FCSTD DOCUMENT  (FreeCAD 0.21R33771 (Git))
Label: Master_of_Puppets
License: All rights reserved
LicenseURL: https://en.wikipedia.org/wiki/All_rights_reserved
objects: Spreadsheet::Sheet×10

FEATURE [Spreadsheet::Sheet] Spreadsheet
  cells = A1='MagnAFPM; A2='RotorDiameter; B2(RotorDiameter)=1200; A3='RotorDiskRadius; B3(RotorDiskRadius)=80.05; A4='RotorDiskInnerRadius; B4(RotorDiskInnerRadius)=54.89; A5='RotorDiskThickness; B5(RotorDiskThickness)=5; A6='MagnetLength; B6(MagnetLength)=25; A7='MagnetWidth; B7(MagnetWidth)=10; A8='MagnetThickness; B8(MagnetThickness)=8; A9='MagnetMaterial; B9(MagnetMaterial)='Neodymium; A10='NumberMagnet; B10(NumberMagnet)=16; A11='StatorThickness; B11(StatorThickness)=8; A12='CoilType; B12(CoilType)=1; A13='CoilLegWidth; B13(CoilLegWidth)=9.36; A14='CoilHoleWidthAtOuterRadius; B14(CoilHoleWidthAtOuterRadius)=10; A15='CoilHoleWidthAtInnerRadius; B15(CoilHoleWidthAtInnerRadius)=10; A16='MechanicalClearance; B16(MechanicalClearance)=3; A17='InnerDistanceBetweenMagnets; B17(InnerDistanceBetweenMagnets)=11.56; A18='NumberOfCoilsPerPhase; B18(NumberOfCoilsPerPhase)=4; A19='WireWeight; B19(WireWeight)=0.46; A20='WireDiameter; B20(WireDiameter)=0.71; A21='NumberOfWiresInHand; B21(NumberOfWiresInHand)=1; A22='TurnsPerCoil; B22(TurnsPerCoil)=103; A23='Furling; A24='VerticalPlaneAngle; B24(VerticalPlaneAngle)=15; A25='HorizontalPlaneAngle; B25(HorizontalPlaneAngle)=55; A26='BracketLength; B26(BracketLength)=150; A27='BracketWidth; B27(BracketWidth)=20; A28='BracketThickness; B28(BracketThickness)=5; A29='BoomLength; B29(BoomLength)=700; A30='BoomPipeDiameter; B30(BoomPipeDiameter)=33.4; A31='BoomPipeThickness; B31(BoomPipeThickness)=3; A32='VaneThickness; B32(VaneThickness)=6; A33='VaneLength; B33(VaneLength)=500; A34='VaneWidth; B34(VaneWidth)=200; A35='Offset; B35(Offset)=69; A36='User; A37='BladeWidth; B37(BladeWidth)=140; A38='HubPitchCircleDiameter; B38(HubPitchCircleDiameter)=50; A39='RotorDiskCentralHoleDiameter; B39(RotorDiskCentralHoleDiameter)=35; A40='HolesDiameter; B40(HolesDiameter)=8; A41='MetalLengthL; B41(MetalLengthL)=40; A42='MetalThicknessL; B42(MetalThicknessL)=5; A43='FlatMetalThickness; B43(FlatMetalThickness)=5; A44='YawPipeDiameter; B44(YawPipeDiameter)=48.3; A45='PipeThickness; B45(PipeThickness)=3; A46='RotorResinMargin; B46(RotorResinMargin)=5; A47='HubHolesDiameter; B47(HubHolesDiameter)=8
FEATURE [Spreadsheet::Sheet] Fastener
  cells = A1='Inputs; A2='BracketThickness; B2(BracketThickness)==Spreadsheet.BracketThickness; A3='VaneThickness; B3(VaneThickness)==Spreadsheet.VaneThickness; A4='FlatMetalThickness; B4(FlatMetalThickness)==Spreadsheet.FlatMetalThickness; A5='HolesDiameter; B5(HolesDiameter)==Spreadsheet.HolesDiameter; A6='HubHolesDiameter; B6(HubHolesDiameter)==Spreadsheet.HubHolesDiameter; A7='Static; A8='HolesRadius; B8(HolesRadius)==HolesDiameter / 2; A9='HubHolesRadius; B9(HubHolesRadius)==HubHolesDiameter / 2; A10='HexNutThickness; B10(HexNutThickness)==1.64 * HolesRadius + 0.35; A11='HubHexNutThickness; B11(HubHexNutThickness)==1.64 * HubHolesRadius + 0.35; A12='WasherThickness; B12(WasherThickness)=2.5; A13='DistanceThreadsExtendFromNuts; B13(DistanceThreadsExtendFromNuts)=5; A14='HubHolesBoltLength; B14(HubHolesBoltLength)=50; A15='WoodScrewDiameter; B15(WoodScrewDiameter)=5; A16='ScrewHoleDiameter; B16(ScrewHoleDiameter)==WoodScrewDiameter - 1; A17='Calculated; A18='UnroundedTailVaneBracketBoltLength; B18(UnroundedTailVaneBracketBoltLength)==BracketThickness + VaneThickness + FlatMetalThickness + DistanceThreadsExtendFromNuts + WasherThickness; A19='TailVaneBracketBoltLength; B19(TailVaneBracketBoltLength)==UnroundedTailVaneBracketBoltLength + 5 - mod(UnroundedTailVaneBracketBoltLength; 5); A20='HolesWidthAcrossCorners; B20='Select C (MAX) based on HolesRadius.; C20='https://www.atlrod.com/metric-hex-bolt-dimensions/; A21='HWACrange7; B21(HWACrange7)==HolesRadius <= 18 ? 63.51 : 75.05; A22='HWACrange6; B22(HWACrange6)==HolesRadius <= 15 ? 53.12 : HWACrange7; A23='HWACrange5; B23(HWACrange5)==HolesRadius <= 12 ? 41.57 : HWACrange6; A24='HWACrange4; B24(HWACrange4)==HolesRadius <= 10 ? 34.64 : HWACrange5; A25='HWACrange3; B25(HWACrange3)==HolesRadius <= 8 ? 27.71 : HWACrange4; A26='HWACrange2; B26(HWACrange2)==HolesRadius <= 7 ? 24.25 : HWACrange3; A27='HWACrange1; B27(HWACrange1)==HolesRadius <= 6 ? 20.78 : HWACrange2; A28='HolesWidthAcrossCorners; B28(HolesWidthAcrossCorners)==HolesRadius <= 5 ? 18.48 : HWACrange1; A29='HubHolesWidthAcrossCorners; B29='Select C (MAX) based on HubHolesRadius.; C29='https://www.atlrod.com/metric-hex-bolt-dimensions/; A30='HHWACrange7; B30(HHWACrange7)==HubHolesRadius <= 18 ? 63.51 : 75.05; A31='HHWACrange6; B31(HHWACrange6)==HubHolesRadius <= 15 ? 53.12 : HHWACrange7; A32='HHWACrange5; B32(HHWACrange5)==HubHolesRadius <= 12 ? 41.57 : HHWACrange6; A33='HHWACrange4; B33(HHWACrange4)==HubHolesRadius <= 10 ? 34.64 : HHWACrange5; A34='HHWACrange3; B34(HHWACrange3)==HubHolesRadius <= 8 ? 27.71 : HHWACrange4; A35='HHWACrange2; B35(HHWACrange2)==HubHolesRadius <= 7 ? 24.25 : HHWACrange3; A36='HHWACrange1; B36(HHWACrange1)==HubHolesRadius <= 6 ? 20.78 : HHWACrange2; A37='HubHolesWidthAcrossCorners; B37(HubHolesWidthAcrossCorners)==HubHolesRadius <= 5 ? 18.48 : HHWACrange1
FEATURE [Spreadsheet::Sheet] Hub
  cells = A1='Inputs; A2='Spreadsheet; A3='RotorDiskRadius; B3='HubPitchCircleDiameter; C3='HubHolesDiameter; A4(RotorDiskRadius)==Spreadsheet.RotorDiskRadius; B4(HubPitchCircleDiameter)==Spreadsheet.HubPitchCircleDiameter; C4(HubHolesDiameter)==Spreadsheet.HubHolesDiameter; A5='MetalLengthL; B5='RotorDiskCentralHoleDiameter; A6(MetalLengthL)==Spreadsheet.MetalLengthL; B6(RotorDiskCentralHoleDiameter)==Spreadsheet.RotorDiskCentralHoleDiameter; A7='Fastener; A8='HubHexNutThickness; A9(HubHexNutThickness)==Fastener.HubHexNutThickness; A10='Common; A11='CoverThickness; A12(CoverThickness)=10; A13='Calculated; A14='RotorDiskCentralHoleRadius; B14='HubHolesRadius; C14='HubPitchCircleRadius; A15(RotorDiskCentralHoleRadius)==RotorDiskCentralHoleDiameter / 2; B15(HubHolesRadius)==HubHolesDiameter / 2; C15(HubPitchCircleRadius)==HubPitchCircleDiameter / 2; A16='Dimensions; D17='FrameSidePad; F17='RotorSidePad; B18='MiddlePadRadiusMargin; C18='ProtrudingPadThickness; D18='Radius; E18='Width; F18='Radius; G18='Width; H18='NumberOfHoles; I18='StubAxleShaftRadius; A19='TShape; B19(TShapeMiddlePadRadiusMargin)=15; C19(TShapeProtrudingPadThickness)=5; D19(TShapeFrameSidePadRadius)=32.5; E19(TShapeFrameSidePadWidth)=45; F19(TShapeRotorSidePadRadius)=28; G19(TShapeRotorSidePadWidth)=40; H19(TShapeNumberOfHoles)=4; I19(TShapeStubAxleShaftRadius)=18; A20='HShape; B20(HShapeMiddlePadRadiusMargin)=15; C20(HShapeProtrudingPadThickness)=5; D20(HShapeFrameSidePadRadius)=42.5; E20(HShapeFrameSidePadWidth)=45; F20(HShapeRotorSidePadRadius)=31; G20(HShapeRotorSidePadWidth)=40; H20(HShapeNumberOfHoles)=5; I20(HShapeStubAxleShaftRadius)=22.5; A21='StarShape; B21(StarShapeMiddlePadRadiusMargin)=20; C21(StarShapeProtrudingPadThickness)=10; D21(StarShapeFrameSidePadRadius)=52.5; E21(StarShapeFrameSidePadWidth)=55; F21(StarShapeRotorSidePadRadius)=47.5; G21(StarShapeRotorSidePadWidth)=75; H21(StarShapeNumberOfHoles)=6; I21(StarShapeStubAxleShaftRadius)=30; A22='Default Value; B22(MiddlePadRadiusMargin)==RotorDiskRadius < 187.5 ? TShapeMiddlePadRadiusMargin : (RotorDiskRadius < 275 ? HShapeMiddlePadRadiusMargin : StarShapeMiddlePadRadiusMargin); C22(ProtrudingPadThickness)==RotorDiskRadius < 187.5 ? TShapeProtrudingPadThickness : (RotorDiskRadius < 275 ? HShapeProtrudingPadThickness : StarShapeProtrudingPadThickness); D22(FrameSidePadRadius)==RotorDiskRadius < 187.5 ? TShapeFrameSidePadRadius : (RotorDiskRadius < 275 ? HShapeFrameSidePadRadius : StarShapeFrameSidePadRadius); E22(FrameSidePadWidth)==RotorDiskRadius < 187.5 ? TShapeFrameSidePadWidth : (RotorDiskRadius < 275 ? HShapeFrameSidePadWidth : StarShapeFrameSidePadWidth); F22(DefaultRotorSidePadRadius)==RotorDiskRadius < 187.5 ? TShapeRotorSidePadRadius : (RotorDiskRadius < 275 ? HShapeRotorSidePadRadius : StarShapeRotorSidePadRadius); G22(RotorSidePadWidth)==RotorDiskRadius < 187.5 ? TShapeRotorSidePadWidth : (RotorDiskRadius < 275 ? HShapeRotorSidePadWidth : StarShapeRotorSidePadWidth); H22(NumberOfHoles)==RotorDiskRadius < 187.5 ? TShapeNumberOfHoles : (RotorDiskRadius < 275 ? HShapeNumberOfHoles : StarShapeNumberOfHoles); I22(StubAxleShaftRadius)==RotorDiskRadius < 187.5 ? TShapeStubAxleShaftRadius : (RotorDiskRadius < 275 ? HShapeStubAxleShaftRadius : StarShapeStubAxleShaftRadius); A23='Value; F23(RotorSidePadRadius)==DefaultRotorSidePadRadius >= RotorDiskCentralHoleRadius ? RotorDiskCentralHoleRadius - 3 : DefaultRotorSidePadRadius; A24='MiddlePad; A25='Radius; B25='Thickness; A26(MiddlePadRadius)==HubPitchCircleRadius + HubHolesRadius + MiddlePadRadiusMargin; B26(MiddlePadThickness)=16; A27='StubAxleShaft; A28='LengthOfTwoNuts; B28='DistanceStubAxleShaftExtendsBeyondTheFrame; C28='DistanceBetweenFrameAndBackRotor; D28='Length; A29(LengthOfTwoNuts)==HubHexNutThickness * 2; B29(DistanceStubAxleShaftExtendsBeyondTheFrame)=20; C29(DistanceBetweenFrameAndBackRotor)==MiddlePadThickness + LengthOfTwoNuts; D29(StubAxleShaftLength)==DistanceBetweenFrameAndBackRotor + MetalLengthL + DistanceStubAxleShaftExtendsBeyondTheFrame
FEATURE [Spreadsheet::Sheet] Blade
  cells = A1='Inputs; A2='Spreadsheet; A3='RotorDiameter; B3='BladeWidth; C3='HubPitchCircleDiameter; A4(RotorDiameter)==Spreadsheet.RotorDiameter; B4(BladeWidth)==Spreadsheet.BladeWidth; C4(HubPitchCircleDiameter)==Spreadsheet.HubPitchCircleDiameter; A5='HubHolesDiameter; B5='ScrewHoleDiameter; A6(HubHolesDiameter)==Spreadsheet.HubHolesDiameter; B6(ScrewHoleDiameter)==Fastener.ScrewHoleDiameter; A7='Static; A8='BladeTemplateThickness; A9(BladeTemplateThickness)=6; A10='Calculated; A11='HubPitchCircleRadius; B11='HubHolesRadius; C11='ScrewHoleRadius; A12(HubPitchCircleRadius)==HubPitchCircleDiameter / 2; B12(HubHolesRadius)==HubHolesDiameter / 2; C12(ScrewHoleRadius)==ScrewHoleDiameter / 2; A13='BladeRadius; B13='MinimumBladeWidth; A14(BladeRadius)==RotorDiameter / 2; B14(MinimumBladeWidth)==max(round(0.055 * RotorDiameter - 8); 95); A15='BladeAssemblyBackDiskDiameter; B15='BladeAssemblyFrontTriangleSideLength; A16(BladeAssemblyBackDiskDiameter)==max(round(0.106 * RotorDiameter - 3.121); 200); B16(BladeAssemblyFrontTriangleSideLength)==max(round(0.147 * RotorDiameter + 6.213); 274); A17='BladeTemplateDim_V; B17='BladeTemplateDim_W; A18(BladeTemplateDim_V)==max(round(0.086 * RotorDiameter - 10.669); 140); B18(BladeTemplateDim_W)==round(0.018 * RotorDiameter + 12.986); A19='UnroundedBladeAssemblyPlateThickness; A20(UnroundedBladeAssemblyPlateThickness)==0.004 * RotorDiameter + 2.426; A21='BladeAssemblyPlateThickness; B21='Round to nearest plywood thickness; A22='Range7; B22(Range7)==UnroundedBladeAssemblyPlateThickness < 28.5 ? 27 : 30; A23='Range6; B23(Range6)==UnroundedBladeAssemblyPlateThickness < 25.5 ? 24 : Range7; A24='Range5; B24(Range5)==UnroundedBladeAssemblyPlateThickness < 22.5 ? 21 : Range6; A25='Range4; B25(Range4)==UnroundedBladeAssemblyPlateThickness < 19.5 ? 18 : Range5; A26='Range3; B26(Range3)==UnroundedBladeAssemblyPlateThickness < 16.5 ? 15 : Range4; A27='Range2; B27(Range2)==UnroundedBladeAssemblyPlateThickness < 13.5 ? 12 : Range3; A28='BladeAssemblyPlateThickness; B28(BladeAssemblyPlateThickness)==UnroundedBladeAssemblyPlateThickness < 10.5 ? 9 : Range2; A29='TotalNumberOfBladeScrews; B29='UnroundedMinimumNumberOfFrontTriangleScrews; C29='UnroundedNumberOfBackDiskScrews; A30(TotalNumberOfBladeScrews)==max(round(0.013 * RotorDiameter + 16.929); 42); B30(UnroundedMinimumNumberOfFrontTriangleScrews)==TotalNumberOfBladeScrews * 0.48; C30(UnroundedNumberOfBackDiskScrews)==TotalNumberOfBladeScrews - UnroundedMinimumNumberOfFrontTriangleScrews; A31='MinimumNumberOfFrontTriangleScrews; B31='NumberOfBackDiskScrews; A32(MinimumNumberOfFrontTriangleScrews)==UnroundedMinimumNumberOfFrontTriangleScrews + 3 - mod(UnroundedMinimumNumberOfFrontTriangleScrews; 3); B32(NumberOfBackDiskScrews)==UnroundedNumberOfBackDiskScrews + 3 - mod(UnroundedNumberOfBackDiskScrews; 3); A33='MinimumNumberOfFrontTriangleScrewsPerBlade; B33='NumberOfBackDiskScrewsPerBlade; A34(MinimumNumberOfFrontTriangleScrewsPerBlade)==MinimumNumberOfFrontTriangleScrews / 3; B34(NumberOfBackDiskScrewsPerBlade)==NumberOfBackDiskScrews / 3; A35='LessThan3000; B35='GreaterThanOrEqualTo3000; C35='BladeThickness; A36(LessThan3000)==round(RotorDiameter * 0.0083333333333 + 20); B36(GreaterThanOrEqualTo3000)==round(RotorDiameter * 0.025 - 30); C36(BladeThickness)==max(RotorDiameter < 3000 ? LessThan3000 : GreaterThanOrEqualTo3000; 35); A37='UnroundedBladeAssemblyScrewLength; B37='BladeAssemblyScrewLength; A38(UnroundedBladeAssemblyScrewLength)==(BladeAssemblyPlateThickness * 2 + BladeThickness) / 2; B38(BladeAssemblyScrewLength)==round(UnroundedBladeAssemblyScrewLength - mod(UnroundedBladeAssemblyScrewLength; 5)); A39='Front Triangle Screw Calculations; A40='DistanceFromCenter; B40(DistanceFromCenter)==BladeWidth - BladeTemplateDim_W; A41='MinimumDistanceFromCenter; B41(MinimumDistanceFromCenter)==MinimumBladeWidth - BladeTemplateDim_W; A42='HalfScrewsPerBlade; B42(HalfScrewsPerBlade)==round(MinimumNumberOfFrontTriangleScrewsPerBlade * 0.5); A43='MinimumNumberOfInnerScrews; B43(MinimumNumberOfInnerScrews)==min(HalfScrewsPerBlade; MinimumNumberOfFrontTriangleScrewsPerBlade - HalfScrewsPerBlade); A44='MinimumNumberOfOuterScrews; B44(MinimumNumberOfOuterScrews)==MinimumNumberOfFrontTriangleScrewsPerBlade - MinimumNumberOfInnerScrews; A45='TriangleHeight; B45(TriangleHeight)==BladeAssemblyFrontTriangleSideLength * sqrt(3) / 2; A46='InscribedCircleRadius; B46(InscribedCircleRadius)==TriangleHeight / 3; A47='LargeDistanceBetweenScrewHolesCircumradii; B47='SmallDistanceBetweenScrewHolesCircumradii; A48(LargeDistanceBetweenScrewHolesCircumradii)==(InscribedCircleRadius - ScrewHoleRadius - (HubPitchCircleRadius + HubHolesRadius)) / 3; B48(SmallDistanceBetweenScrewHolesCircumradii)==(InscribedCircleRadius - ScrewHoleRadius - HubPitchCircleRadius) / 2; A49='TriangleCenterToVertexDistance; B49(TriangleCenterToVertexDistance)==TriangleHeight * 2 / 3; A50='LargeInnerScrewLineDistanceFromCenter; B50='SmallInnerScrewLineDistanceFromCenter; A51(LargeInnerScrewLineDistanceFromCenter)==HubPitchCircleRadius + HubHolesRadius + LargeDistanceBetweenScrewHolesCircumradii; B51(SmallInnerScrewLineDistanceFromCenter)==HubPitchCircleRadius; A52='LargeOuterScrewLineDistanceFromCenter; B52='SmallOuterScrewLineDistanceFromCenter; A53(LargeOuterScrewLineDistanceFromCenter)==LargeInnerScrewLineDistanceFromCenter + ScrewHoleRadius + LargeDistanceBetweenScrewHolesCircumradii; B53(SmallOuterScrewLineDistanceFromCenter)==SmallInnerScrewLineDistanceFromCenter + ScrewHoleRadius + SmallDistanceBetweenScrewHolesCircumradii; A54='DistanceBetweenOuterScrewAndEdge; B54(DistanceBetweenOuterScrewAndEdge)==InscribedCircleRadius - (LargeOuterScrewLineDistanceFromCenter + ScrewHoleRadius); A55='HideInnerScrews; B55(HideInnerScrews)==DistanceBetweenOuterScrewAndEdge < 10 ? 1 : 0; A56='InnerScrewLineDistanceFromCenter; B56(InnerScrewLineDistanceFromCenter)==HideInnerScrews == 1 ? SmallInnerScrewLineDistanceFromCenter : LargeInnerScrewLineDistanceFromCenter; A57='OuterScrewLineDistanceFromCenter; B57(OuterScrewLineDistanceFromCenter)==HideInnerScrews == 1 ? SmallOuterScrewLineDistanceFromCenter : LargeOuterScrewLineDistanceFromCenter; A58='Alpha; B58(Alpha)==acos(BladeTemplateDim_W / TriangleCenterToVertexDistance); A59='Beta; B59(Beta)==180 deg - 60 deg - Alpha; A60='Gamma; B60(Gamma)==180 deg - 90 deg - Beta; A61='InnerScrewBetaHypotenuse; B61(InnerScrewBetaHypotenuse)==InnerScrewLineDistanceFromCenter / cos(Beta); C61='OuterScrewBetaHypotenuse; D61(OuterScrewBetaHypotenuse)==OuterScrewLineDistanceFromCenter / cos(Beta); A62='InnerScrewLineTriangle_Adjacent; B62(InnerScrewLineTriangle_Adjacent)==InnerScrewBetaHypotenuse + BladeTemplateDim_W; C62='OuterScrewLineTriangle_Adjacent; D62(OuterScrewLineTriangle_Adjacent)==OuterScrewBetaHypotenuse + BladeTemplateDim_W; A63='InnerScrewLineTriangle_Hypotenuse; B63(InnerScrewLineTriangle_Hypotenuse)==InnerScrewLineTriangle_Adjacent / cos(Gamma); C63='OuterScrewLineTriangle_Hypotenuse; D63(OuterScrewLineTriangle_Hypotenuse)==OuterScrewLineTriangle_Adjacent / cos(Gamma); A64='InnerScrewGammaAdjacent; B64(InnerScrewGammaAdjacent)==max(InnerScrewBetaHypotenuse - DistanceFromCenter; 0); C64='OuterScrewGammaAdjacent; D64(OuterScrewGammaAdjacent)==max(OuterScrewBetaHypotenuse - DistanceFromCenter; 0); A65='InnerScrewGammaHypotenuse; B65(InnerScrewGammaHypotenuse)==InnerScrewGammaAdjacent / cos(Gamma); C65='OuterScrewGammaHypotenuse; D65(OuterScrewGammaHypotenuse)==OuterScrewGammaAdjacent / cos(Gamma); A66='InnerScrewGammaOpposite; B66(InnerScrewGammaOpposite)==sqrt(InnerScrewGammaHypotenuse ^ 2 - InnerScrewGammaAdjacent ^ 2); C66='OuterScrewGammaOpposite; D66(OuterScrewGammaOpposite)==sqrt(OuterScrewGammaHypotenuse ^ 2 - OuterScrewGammaAdjacent ^ 2); A67='MinimumInnerScrewGammaAdjacent; B67(MinimumInnerScrewGammaAdjacent)==max(InnerScrewBetaHypotenuse - MinimumDistanceFromCenter; 0); C67='MinimumOuterScrewGammaAdjacent; D67(MinimumOuterScrewGammaAdjacent)==max(OuterScrewBetaHypotenuse - MinimumDistanceFromCenter; 0); A68='MinimumInnerScrewGammaHypotenuse; B68(MinimumInnerScrewGammaHypotenuse)==MinimumInnerScrewGammaAdjacent / cos(Gamma); C68='MinimumOuterScrewGammaHypotenuse; D68(MinimumOuterScrewGammaHypotenuse)==MinimumOuterScrewGammaAdjacent / cos(Gamma); A69='MinimumInnerScrewGammaOpposite; B69(MinimumInnerScrewGammaOpposite)==sqrt(MinimumInnerScrewGammaHypotenuse ^ 2 - MinimumInnerScrewGammaAdjacent ^ 2); C69='MinimumOuterScrewGammaOpposite; D69(MinimumOuterScrewGammaOpposite)==sqrt(MinimumOuterScrewGammaHypotenuse ^ 2 - MinimumOuterScrewGammaAdjacent ^ 2); A70='BladeTemplateTrailingEdgeAngle; B70(BladeTemplateTrailingEdgeAngle)==atan(BladeRadius / (BladeWidth - BladeTemplateDim_W)); A71='MinimumBladeTemplateTrailingEdgeAngle; B71(MinimumBladeTemplateTrailingEdgeAngle)==atan(BladeRadius / (MinimumBladeWidth - BladeTemplateDim_W)); A72='Epsilon; B72(Epsilon)==90 deg - BladeTemplateTrailingEdgeAngle; A73='MinimumEpsilon; B73(MinimumEpsilon)==90 deg - MinimumBladeTemplateTrailingEdgeAngle; A74='Delta; B74(Delta)==InnerScrewGammaHypotenuse == 0 ? 0 deg : asin(InnerScrewGammaAdjacent / InnerScrewGammaHypotenuse); A75='DeltaSupplementaryAngle; B75(DeltaSupplementaryAngle)==180 deg - Delta; A76='Zeta; B76(Zeta)==180 deg - DeltaSupplementaryAngle - Epsilon; A77='MinimumDelta; B77(MinimumDelta)==asin(MinimumInnerScrewGammaAdjacent / MinimumInnerScrewGammaHypotenuse); A78='MinimumDeltaSupplementaryAngle; B78(MinimumDeltaSupplementaryAngle)==180 deg - MinimumDelta; A79='MinimumZeta; B79(MinimumZeta)==180 deg - MinimumDeltaSupplementaryAngle - MinimumEpsilon; A80='InnerScrewHypotenuseAddition; B80(InnerScrewHypotenuseAddition)==InnerScrewGammaOpposite / sin(Zeta) * sin(Epsilon); C80='OuterScrewHypotenuseAddition; D80(OuterScrewHypotenuseAddition)==OuterScrewGammaOpposite / sin(Zeta) * sin(Epsilon); A81='MinimumInnerScrewHypotenuseAddition; B81(MinimumInnerScrewHypotenuseAddition)==MinimumInnerScrewGammaOpposite / sin(MinimumZeta) * sin(MinimumEpsilon); C81='MinimumOuterScrewHypotenuseAddition; D81(MinimumOuterScrewHypotenuseAddition)==MinimumOuterScrewGammaOpposite / sin(MinimumZeta) * sin(MinimumEpsilon); A82='InnerScrewHypotenuseOffset; B82(InnerScrewHypotenuseOffset)==InnerScrewGammaHypotenuse + InnerScrewHypotenuseAddition; C82='OuterScrewHypotenuseOffset; D82(OuterScrewHypotenuseOffset)==OuterScrewGammaHypotenuse + OuterScrewHypotenuseAddition; A83='MinimumInnerScrewHypotenuseOffset; B83(MinimumInnerScrewHypotenuseOffset)==MinimumInnerScrewGammaHypotenuse + MinimumInnerScrewHypotenuseAddition; C83='MinimumOuterScrewHypotenuseOffset; D83(MinimumOuterScrewHypotenuseOffset)==MinimumOuterScrewGammaHypotenuse + MinimumOuterScrewHypotenuseAddition; A84='InnerScrewHypotenuseOffsetDifference; B84(InnerScrewHypotenuseOffsetDifference)==MinimumInnerScrewHypotenuseOffset - InnerScrewHypotenuseOffset; C84='OuterScrewHypotenuseOffsetDifference; D84(OuterScrewHypotenuseOffsetDifference)==MinimumOuterScrewHypotenuseOffset - OuterScrewHypotenuseOffset; A85='InnerScrewLineHypotenuse; B85(InnerScrewLineHypotenuse)==InnerScrewLineTriangle_Hypotenuse - InnerScrewHypotenuseOffset; C85='OuterScrewLineHypotenuse; D85(OuterScrewLineHypotenuse)==OuterScrewLineTriangle_Hypotenuse - OuterScrewHypotenuseOffset; A86='MaximumDistanceBetweenInnerScrews; +23 more cells
FEATURE [Spreadsheet::Sheet] Alternator
  cells = A1='Inputs; A2='Spreadsheet; A3='RotorDiskRadius; B3='StatorThickness; C3='MechanicalClearance; A4(RotorDiskRadius)==Spreadsheet.RotorDiskRadius; B4(StatorThickness)==Spreadsheet.StatorThickness; C4(MechanicalClearance)==Spreadsheet.MechanicalClearance; A5='RotorDiskThickness; B5='MagnetThickness; C5='MagnetLength; A6(RotorDiskThickness)==Spreadsheet.RotorDiskThickness; B6(MagnetThickness)==Spreadsheet.MagnetThickness; C6(MagnetLength)==Spreadsheet.MagnetLength; A7='MetalLengthL; B7='MetalThicknessL; C7='CoilLegWidth; A8(MetalLengthL)==Spreadsheet.MetalLengthL; B8(MetalThicknessL)==Spreadsheet.MetalThicknessL; C8(CoilLegWidth)==Spreadsheet.CoilLegWidth; A9='Offset; B9='HolesDiameter; C9='YawPipeDiameter; A10(Offset)==Spreadsheet.Offset; B10(HolesDiameter)==Spreadsheet.HolesDiameter; C10(YawPipeDiameter)==Spreadsheet.YawPipeDiameter; A11='RotorResinMargin; B11='NumberMagnet; C11='HubHolesDiameter; A12(RotorResinMargin)==Spreadsheet.RotorResinMargin; B12(NumberMagnet)==Spreadsheet.NumberMagnet; C12(HubHolesDiameter)==Spreadsheet.HubHolesDiameter; A13='CoilHoleWidthAtOuterRadius; B13='CoilHoleWidthAtInnerRadius; C13='CoilType; A14(CoilHoleWidthAtOuterRadius)==Spreadsheet.CoilHoleWidthAtOuterRadius; B14(CoilHoleWidthAtInnerRadius)==Spreadsheet.CoilHoleWidthAtInnerRadius; C14(CoilType)==Spreadsheet.CoilType; A15='MagnetMaterial; B15='NumberOfCoilsPerPhase; C15='MagnetWidth; A16(MagnetMaterial)==Spreadsheet.MagnetMaterial; B16(NumberOfCoilsPerPhase)==Spreadsheet.NumberOfCoilsPerPhase; C16(MagnetWidth)==Spreadsheet.MagnetWidth; A17='Hub; A18='DistanceBetweenFrameAndBackRotor; B18='NumberOfHoles; C18='HubHolesRadius; A19(DistanceBetweenFrameAndBackRotor)==Hub.DistanceBetweenFrameAndBackRotor; B19(NumberOfHoles)==Hub.NumberOfHoles; C19(HubHolesRadius)==Hub.HubHolesRadius; A20='HubPitchCircleRadius; B20='MiddlePadThickness; A21(HubPitchCircleRadius)==Hub.HubPitchCircleRadius; B21(MiddlePadThickness)==Hub.MiddlePadThickness; A22='Fastener; A23='HexNutThickness; B23='HubHexNutThickness; C23='DistanceThreadsExtendFromNuts; D23='WasherThickness; A24(HexNutThickness)==Fastener.HexNutThickness; B24(HubHexNutThickness)==Fastener.HubHexNutThickness; C24(DistanceThreadsExtendFromNuts)==Fastener.DistanceThreadsExtendFromNuts; D24(WasherThickness)==Fastener.WasherThickness; A25='ScrewHoleDiameter; A26(ScrewHoleDiameter)==Fastener.ScrewHoleDiameter; A27='Blade; A28='BladeAssemblyPlateThickness; B28='BladeThickness; A29(BladeAssemblyPlateThickness)==Blade.BladeAssemblyPlateThickness; B29(BladeThickness)==Blade.BladeThickness; A30='Static; A31='AlternatorTiltAngle; B31(AlternatorTiltAngle)==4 deg; C31='See right-hand side of page 29 of "A Wind Turbine Recipe Book (2014)".; A32='Stator; A33='HexagonalStatorOuterCircumradius; B33='StatorInnerHoleRadius; C33='NumberOfCoils; A34(HexagonalStatorOuterCircumradius)==(RotorDiskRadius + CoilLegWidth + 20) / cos(30); B34(StatorInnerHoleRadius)==RotorDiskRadius - MagnetLength - OffsetToAlignCornersOfMagnetToDisk - CoilLegWidth; C34(NumberOfCoils)==NumberMagnet * 0.75; A35='TShapeStatorHolesCircumradius; B35='HShapeStatorHolesCircumradius; C35='StarShapeStatorHolesCircumradius; D35='StatorHolesCircumradius; A36(TShapeStatorHolesCircumradius)==RotorDiskRadius + CoilLegWidth + 20; B36(HShapeStatorHolesCircumradius)==TShapeStatorHolesCircumradius + HolesRadius; C36(StarShapeStatorHolesCircumradius)==RotorDiskRadius + CoilLegWidth + 0.5 * (HexagonalStatorOuterCircumradius - RotorDiskRadius - CoilLegWidth); D36(StatorHolesCircumradius)==RotorDiskRadius < 187.5 ? TShapeStatorHolesCircumradius : (RotorDiskRadius < 275 ? HShapeStatorHolesCircumradius : StarShapeStatorHolesCircumradius); A37='TShapeNumberOfStatorHoles; B37='HShapeNumberOfStatorHoles; C37='StarShapeNumberOfStatorHoles; D37='NumberOfStatorHoles; A38(TShapeNumberOfStatorHoles)=3; B38(HShapeNumberOfStatorHoles)=4; C38(StarShapeNumberOfStatorHoles)=6; D38(NumberOfStatorHoles)==RotorDiskRadius < 187.5 ? TShapeNumberOfStatorHoles : (RotorDiskRadius < 275 ? HShapeNumberOfStatorHoles : StarShapeNumberOfStatorHoles); A39='TShapeEarSize; B39='HShapeEarSize; C39='EarSize; A40(TShapeEarSize)=25; B40(HShapeEarSize)=35; C40(EarSize)==RotorDiskRadius < 187.5 ? TShapeEarSize : HShapeEarSize; A41='TAndStarShapeCoilsAngle; B41='HShapeCoilsAngle; C41='CoilsAngle; A42(TAndStarShapeCoilsAngle)==360 / NumberOfCoils / 2; B42(HShapeCoilsAngle)=0; C42(CoilsAngle)==RotorDiskRadius < 187.5 ? TAndStarShapeCoilsAngle : (RotorDiskRadius < 275 ? HShapeCoilsAngle : TAndStarShapeCoilsAngle); A43='CoilThicknessOffset; B43='CoilThickness; A44(CoilThicknessOffset)=0.2; B44(CoilThickness)==StatorThickness - CoilThicknessOffset; A45='Mold; A46='StatorMoldBoltDiameter; B46='StatorMoldBoltWidthAcrossCorners; C46='StatorMoldBoltLength; A47(StatorMoldBoltDiameter)=12; B47(StatorMoldBoltWidthAcrossCorners)=20.78; C47(StatorMoldBoltLength)=65; A48='LocatingBoltDiameter; B48='LocatingBoltLength; A49(LocatingBoltDiameter)=12; B49(LocatingBoltLength)=85; A50='ScrewHoleRadius; B50='DistanceBetweenOuterHolesAndStatorMold; C50='DistanceBetweenInnerHolesAndStatorMold; A51(ScrewHoleRadius)==ScrewHoleDiameter / 2; B51(DistanceBetweenOuterHolesAndStatorMold)==StatorMoldBoltDiameter * 2; C51(DistanceBetweenInnerHolesAndStatorMold)==StatorMoldBoltDiameter * 1.5; A52='TShapeSketchY; B52='HShapeSketchY; C52='SketchY; A53(TShapeSketchY)==-EarSize / 2; B53(HShapeSketchY)=0; C53(SketchY)==RotorDiskRadius < 187.5 ? TShapeSketchY : HShapeSketchY; A54='IslandInnerRadius; B54='EarAngle; C54='StatorMoldSideLength; A55(IslandInnerRadius)==StatorInnerHoleRadius - DistanceBetweenInnerHolesAndStatorMold; B55(EarAngle)==360 / NumberOfStatorHoles; C55(StatorMoldSideLength)==1.55 * 2 * StatorHolesCircumradius; A56='LargeHoleAngle; B56='LengthMiddleHoles; C56='StatorMoldHolesSketchAngle; A57(LargeHoleAngle)==EarAngle / 4; B57(LengthMiddleHoles)==(RotorDiskRadius < 275 ? StatorHolesCircumradius : HexagonalStatorOuterCircumradius) + DistanceBetweenOuterHolesAndStatorMold; C57(StatorMoldHolesSketchAngle)==RotorDiskRadius < 187.5 ? 0 : (RotorDiskRadius < 275 ? 45 : 0); A58='StatorMoldIslandNumberOfBolts; B58='StatorMoldIslandNumberOfScrewSectors; C58='StatorMoldIslandScrewAngle; A59(StatorMoldIslandNumberOfBolts)==RotorDiskRadius < 187.5 ? 4 : (RotorDiskRadius < 275 ? 6 : 12); B59(StatorMoldIslandNumberOfScrewSectors)==RotorDiskRadius < 187.5 ? 12 : (RotorDiskRadius < 275 ? 18 : 36); C59(StatorMoldIslandScrewAngle)==360 deg / StatorMoldIslandNumberOfScrewSectors; A60='StatorMoldIslandNumberOfScrews; B60='DistanceOfLocatingHoleFromCenter; A61(StatorMoldIslandNumberOfScrews)==(StatorMoldIslandNumberOfScrewSectors - StatorMoldIslandNumberOfBolts) / 2; B61(DistanceOfLocatingHoleFromCenter)==0.63559 * StatorMoldSideLength; A62='UnroundedStatorMoldScrewLength; B62='StatorMoldScrewLength; A63(UnroundedStatorMoldScrewLength)==StatorThickness * 2; B63(StatorMoldScrewLength)==UnroundedStatorMoldScrewLength - mod(UnroundedStatorMoldScrewLength; 5); A64='LocatingBolt1X; B64='LocatingBolt1Y; A65(LocatingBolt1X)==-DistanceOfLocatingHoleFromCenter * cos(45); B65(LocatingBolt1Y)==-LocatingBolt1X + SketchY; A66='LocatingBolt2X; B66='LocatingBolt2Y; A67(LocatingBolt2X)==-LocatingBolt1X; B67(LocatingBolt2Y)==LocatingBolt1Y; A68='LocatingBolt3X; B68='LocatingBolt3Y; A69(LocatingBolt3X)==LocatingBolt2X; B69(LocatingBolt3Y)==LocatingBolt1X + SketchY; A70='Hexagonal Mold; A71='TopRightCornerX; B71='TopRightCornerY; A72(TopRightCornerX)==LengthMiddleHoles * cos(60); B72(TopRightCornerY)==LengthMiddleHoles * sin(60); A73='LineFromMiddleRightToTopRightCornerSlope; B73='LineFromMiddleRightToTopRightCornerYIntercept; A74(LineFromMiddleRightToTopRightCornerSlope)==TopRightCornerY / (TopRightCornerX - LengthMiddleHoles); B74(LineFromMiddleRightToTopRightCornerYIntercept)==TopRightCornerY - LineFromMiddleRightToTopRightCornerSlope * TopRightCornerX; A75='CoilWinder; A76='MagnetDiagonal; B76='CoilWinderDiskRadiusPadding; C76='CoilWinderDiskRadius; A77(MagnetDiagonal)==sqrt(MagnetWidth ^ 2 + MagnetLength ^ 2); B77(CoilWinderDiskRadiusPadding)=12; C77(CoilWinderDiskRadius)==MagnetDiagonal / 2 + CoilLegWidth + CoilWinderDiskRadiusPadding; A78='DistanceBetweenTriangularCoilAndTapeNotch; B78='LargestMagnetDimension; C78='SmallestMagnetDimension; A79(DistanceBetweenTriangularCoilAndTapeNotch)=2; B79(LargestMagnetDimension)==max(MagnetLength; MagnetWidth); C79(SmallestMagnetDimension)==min(MagnetLength; MagnetWidth); A80='CoilWinderBoltDiameter; B80='Ensure 2 mm of plywood between bolt hole and tape notch.; A81='CwbRange4; +264 more cells
FEATURE [Spreadsheet::Sheet] YawBearing
  cells = A1='Inputs; A2='Spreadsheet; A3='YawPipeDiameter; B3='FlatMetalThickness; C3='MetalLengthL; A4(YawPipeDiameter)==Spreadsheet.YawPipeDiameter; B4(FlatMetalThickness)==Spreadsheet.FlatMetalThickness; C4(MetalLengthL)==Spreadsheet.MetalLengthL; A5='Offset; B5='RotorDiskRadius; A6(Offset)==Spreadsheet.Offset; B6(RotorDiskRadius)==Spreadsheet.RotorDiskRadius; A7='Alternator; A8='AlternatorTiltAngle; B8='I; A9(AlternatorTiltAngle)==Alternator.AlternatorTiltAngle; B9(I)==Alternator.I; A10='Pipe; A11='ScaleFactor; B11(YawPipeScaleFactor)==RotorDiskRadius < 187.5 ? 0.95 : 0.9; A12='ProjectedLength; B12(YawPipeProjectedLength)==RotorDiskRadius * YawPipeScaleFactor * 2; A13='Plate; A14='CornerChamferLength; B14(YawBearingPlateCornerChamferLength)=10; A15='TopHoleRadius; B15(YawBearingPlateTopHoleRadius)==RotorDiskRadius < 187.5 ? 10 : 17.5; A16='Extended Yaw Bearing (H & Star Shape); A17='SideWidth; B17(SideWidth)==YawPipeProjectedLength * 0.25; A18='TopAngle; B18(TopAngle)==45 deg; A19='Gamma; B19(Gamma)==tan(AlternatorTiltAngle) * SideWidth; A20='Delta; B20(Delta)==cos(TopAngle) * FlatMetalThickness; A21='Epsilon; B21(Epsilon)==Delta * 2; A22='TopFrameJunctionOverhangDistance; B22(TopFrameJunctionOverhangDistance)==Epsilon + Gamma; A23='Mhypotenuse; B23(Mhypotenuse)==MetalLengthL * 2 + TopFrameJunctionOverhangDistance; A24='YawPipeRadius; B24='Madjacent; C24='MM (M); A25(YawPipeRadius)==YawPipeDiameter / 2; B25(Madjacent)==cos(TopAngle) * Mhypotenuse; C25(MM)==Madjacent < YawPipeDiameter ? YawPipeDiameter : Madjacent; A26='MMhypotenuse; A27(MMhypotenuse)==hypot(MM; MM); A28='AlternatorCenterRatio; B28='L; C28='LargeYawBearingXOffset; A29(AlternatorCenterRatio)==(MetalLengthL * 2 - TopFrameJunctionOverhangDistance) / 2 / MMhypotenuse; B29(L)==YawPipeRadius + Offset / cos(TopAngle) + AlternatorCenterRatio * MM; C29(LargeYawBearingXOffset)==TopFrameJunctionOverhangDistance / 2; A30='Side; A31='CanSideExtendToMiddleOfYawBearingPipe; A32(CanSideExtendToMiddleOfYawBearingPipe)==(MM - YawPipeDiameter) / 2 > FlatMetalThickness ? True : False; A33='HalfWidth; B33(HalfWidth)==MM / 2; A34='DistanceBetweenTopAndPipe; B34(DistanceBetweenTopAndPipe)==HalfWidth - YawPipeRadius; A35='DistanceBetweenSideAndPipe; B35(DistanceBetweenSideAndPipe)==CanSideExtendToMiddleOfYawBearingPipe == True ? DistanceBetweenTopAndPipe - FlatMetalThickness : 0; A36='AV; B36(AV)==FlatMetalThickness - DistanceBetweenTopAndPipe > 0 ? FlatMetalThickness - DistanceBetweenTopAndPipe : FlatMetalThickness; A37='VO; B37(VO)==YawPipeRadius - AV; A38='X; B38='Y; C38='Z; A39(SideX)==CanSideExtendToMiddleOfYawBearingPipe == False ? sqrt(YawPipeRadius ^ 2 - VO ^ 2) : 0; B39(SideY)==-SideWidth; C39(SideZ)==-HalfWidth + DistanceBetweenSideAndPipe; A40='SideLength; A41='Adj; B41(Adj)==L - MM - YawPipeRadius; A42='DistanceSideExtendsFromFrameAtJunction; B42(DistanceSideExtendsFromFrameAtJunction)==TopFrameJunctionOverhangDistance - hypot(DistanceBetweenSideAndPipe; DistanceBetweenSideAndPipe); A43='Eta; B43(Eta)==hypot(DistanceSideExtendsFromFrameAtJunction; DistanceSideExtendsFromFrameAtJunction); A44='Theta; B44(Theta)==Eta - FlatMetalThickness; A45='SideYAngle; B45(SideYAngle)==atan(DistanceBetweenSideAndPipe / Adj); A46='Hyp; B46(Hyp)==hypot(DistanceBetweenSideAndPipe; Adj); A47='Iota; B47(Iota)==FlatMetalThickness * tan(TopAngle - SideYAngle); A48='Kappa; B48(Kappa)==FlatMetalThickness / sin(TopAngle + SideYAngle); A49='Lambda; B49(Lambda)==TopFrameJunctionOverhangDistance - Kappa; A50='Zeta; B50(Zeta)==Lambda / cos(TopAngle + SideYAngle); A51='SideLength; B51(SideLength)==CanSideExtendToMiddleOfYawBearingPipe == True ? Hyp + Iota + Zeta : Adj - SideX + DistanceBetweenSideAndPipe + Theta; A52='ArcWireSupport; A53='Thickness; B53='Width; C53='Hole_y; A54(ArcWireSupportThickness)=5; B54(ArcWireSupportWidth)==FlatMetalThickness; C54(Hole_y)==YawPipeRadius + I; A55='SmallLength; B55='LargeLength; C55='Length; A56(ArcWireSupportSmallLength)==Hole_y - YawBearingPlateTopHoleRadius; B56(ArcWireSupportLargeLength)==HalfWidth * sqrt(2) - YawBearingPlateTopHoleRadius - ArcWireSupportWidth / 2; C56(ArcWireSupportLength)==RotorDiskRadius < 187.5 ? ArcWireSupportSmallLength : ArcWireSupportLargeLength
FEATURE [Spreadsheet::Sheet] Tail
  cells = A1='Inputs; A2='Spreadsheet; A3='RotorDiskRadius; B3='BracketLength; C3='FlatMetalThickness; A4(RotorDiskRadius)==Spreadsheet.RotorDiskRadius; B4(BracketLength)==Spreadsheet.BracketLength; C4(FlatMetalThickness)==Spreadsheet.FlatMetalThickness; A5='YawPipeDiameter; B5='VerticalPlaneAngle; C5='HorizontalPlaneAngle; A6(YawPipeDiameter)==Spreadsheet.YawPipeDiameter; B6(VerticalPlaneAngle)==Spreadsheet.VerticalPlaneAngle; C6(HorizontalPlaneAngle)==Spreadsheet.HorizontalPlaneAngle; A7='BoomLength; B7='BoomPipeDiameter; A8(BoomLength)==Spreadsheet.BoomLength; B8(BoomPipeDiameter)==Spreadsheet.BoomPipeDiameter; A9='Calculated; A10='YawPipeRadius; B10='BoomPipeRadius; A11(YawPipeRadius)==YawPipeDiameter / 2; B11(BoomPipeRadius)==BoomPipeDiameter / 2; A12='Hinge; A13='OuterPipe; A14='Diameter; B14(HingeOuterPipeDiameter)==YawPipeDiameter; A15='Radius; B15(HingeOuterPipeRadius)==HingeOuterPipeDiameter / 2; A16='InnerPipe; A17='Diameter; B17='Select one size smaller than outer hinge for inner hinge based on pipe size list.; A18='Range8; B18(Range8_inner)==HingeOuterPipeDiameter <= 141.3 ? 127 : 141.3; A19='Range7; B19(Range7_inner)==HingeOuterPipeDiameter <= 127 ? 114.3 : Range8_inner; A20='Range6; B20(Range6_inner)==HingeOuterPipeDiameter <= 114.3 ? 101.6 : Range7_inner; A21='Range5; B21(Range5_inner)==HingeOuterPipeDiameter <= 101.6 ? 88.9 : Range6_inner; A22='Range4; B22(Range4_inner)==HingeOuterPipeDiameter <= 88.9 ? 73 : Range5_inner; A23='Range3; B23(Range3_inner)==HingeOuterPipeDiameter <= 73 ? 60.3 : Range4_inner; A24='Range2; B24(Range2_inner)==HingeOuterPipeDiameter <= 60.3 ? 48.3 : Range3_inner; A25='Range1; B25(Range1_inner)==HingeOuterPipeDiameter <= 48.3 ? 42.2 : Range2_inner; A26='Diameter; B26(HingeInnerPipeDiameter)==HingeOuterPipeDiameter <= 42.2 ? 33.4 : Range1_inner; A27='Radius; B27(HingeInnerPipeRadius)==HingeInnerPipeDiameter / 2; A28='Length; B28(HingeInnerPipeLength)==0.8 * 2 * RotorDiskRadius; A29='Junction; A30='Height; B30(TailHingeJunctionHeight)==HingeInnerPipeLength / 3; A31='hypotenuse; B31(hypotenuse)==(TailHingeJunctionHeight - FlatMetalThickness) / cos(VerticalPlaneAngle); A32='InnerWidth; B32(TailHingeJunctionInnerWidth)==sqrt(hypotenuse ^ 2 - (TailHingeJunctionHeight - FlatMetalThickness) ^ 2); A33='FullWidth; B33(TailHingeJunctionFullWidth)==YawPipeRadius + HingeInnerPipeRadius + TailHingeJunctionInnerWidth; A34='Chamfer; B34(TailHingeJunctionChamfer)==YawPipeRadius / 2; A35='Tail Hinge Pipe X Z; B35='The following calculations are in the local coordinate space of Tail_Hinge_Inner.; A36='Adjacent; B36(Adjacent)==cos(VerticalPlaneAngle) * HingeInnerPipeRadius; A37='XRotationOffset; B37(XRotationOffset)==HingeInnerPipeRadius - Adjacent; A38='JunctionBottom; B38(JunctionBottom)==TailHingeJunctionHeight - FlatMetalThickness; A39='Opposite; B39(Opposite)==tan(VerticalPlaneAngle) * JunctionBottom; A40='TrigOffset; B40(TrigOffset)==Opposite + XRotationOffset; A41='TailHingePipeX; B41(TailHingePipeX)==YawPipeRadius - TailHingeJunctionChamfer + TailHingeJunctionInnerWidth + HingeInnerPipeRadius - TrigOffset; A42='TailHingePipeZ; B42(TailHingePipeZ)==-HingeInnerPipeRadius * sin(VerticalPlaneAngle); A43='OuterPipe; A44='h1; B44(h1)==-(TailHingePipeZ / cos(VerticalPlaneAngle)); A45='h2; B45(h2)==TailHingeJunctionHeight / cos(VerticalPlaneAngle); A46='DistanceBetweenJunctionAndOuterHinge; B46(DistanceBetweenJunctionAndOuterHinge)=5; A47='Length; B47(HingeOuterPipeLength)==HingeInnerPipeLength - h1 - h2 - DistanceBetweenJunctionAndOuterHinge; A48='Vane Bracket; A49='DistanceToFirstHole; B49(DistanceToFirstHole)==BracketLength / 10; A50='DistanceBetweenHoles; B50(DistanceBetweenHoles)==BracketLength / 2; A51='VaneBracketAngle; B51(VaneBracketAngle)=45; A52='Outer Tail Hinge X Z; A53='PipeHeightOffset; B53(PipeHeightOffset)==HingeInnerPipeLength - HingeOuterPipeLength; A54='XXX; B54(XXX)==sin(VerticalPlaneAngle) * PipeHeightOffset; A55='ZZZ; B55(ZZZ)==cos(VerticalPlaneAngle) * PipeHeightOffset; A56='OuterTailHingeXPosition; B56(OuterTailHingeXPosition)==XXX + TailHingePipeX; A57='OuterTailHingeZPosition; B57(OuterTailHingeZPosition)==ZZZ + TailHingePipeZ; A58='Tail Boom Triangular Brace; A59='BoomPipeTailHingeHypotenuse; B59(BoomPipeTailHingeHypotenuse)==BoomPipeDiameter / sin(90 - VerticalPlaneAngle); A60='DistanceOfBoomFromTopOfOuterTailHinge; B60(DistanceOfBoomFromTopOfOuterTailHinge)=10; A61='HalfHingeOuterPipeLength; B61(HalfHingeOuterPipeLength)==round(HingeOuterPipeLength / 2); A62='DistanceOfOuterHingeBelowBoom; B62(DistanceOfOuterHingeBelowBoom)==HingeOuterPipeLength - DistanceOfBoomFromTopOfOuterTailHinge - BoomPipeTailHingeHypotenuse; A63='TailBoomTriangularBraceWidth; B63(TailBoomTriangularBraceWidth)==RotorDiskRadius < 187.5 ? HalfHingeOuterPipeLength : DistanceOfOuterHingeBelowBoom; A64='TailBoomTriangularBraceLength; B64(TailBoomTriangularBraceLength)==BoomLength / 3; A65='Tail Angle; A66='DefaultTailAngle; B66(DefaultTailAngle)=110; A67='Tail; A68='TailXInitial; B68(TailXInitial)==cos(VerticalPlaneAngle) * HingeOuterPipeRadius; A69='TailZOffset; B69(TailZOffset)==-sin(VerticalPlaneAngle) * HingeOuterPipeRadius; A70='NonRotatedTailX; B70(NonRotatedTailX)==TailXInitial + OuterTailHingeXPosition; A71='OuterTailHingeTruncatedHypotenuse; B71(OuterTailHingeTruncatedHypotenuse)==HingeOuterPipeLength - DistanceOfBoomFromTopOfOuterTailHinge; A72='OuterTailHingeXPositionOffset; B72(OuterTailHingeXPositionOffset)==cos(90 - VerticalPlaneAngle) * OuterTailHingeTruncatedHypotenuse; A73='OuterTailHingeNegativeXOffset; B73(OuterTailHingeNegativeXOffset)==BoomPipeDiameter / tan(90 - VerticalPlaneAngle); A74='NonRotatedTailZ; B74(NonRotatedTailZ)==OuterTailHingeZPosition - BoomPipeRadius + TailZOffset; A75='OuterTailHingeZPositionOffset; B75(OuterTailHingeZPositionOffset)==sin(90 - VerticalPlaneAngle) * OuterTailHingeTruncatedHypotenuse; A76='Point; A77='x; B77='y; C77='z; D77='Vector; A78(PointX)==NonRotatedTailX + OuterTailHingeXPositionOffset - OuterTailHingeNegativeXOffset; B78(PointY)=0; C78(PointZ)==NonRotatedTailZ + OuterTailHingeZPositionOffset; D78(Point)==vector(PointX; PointY; PointZ); A79='Center; A80='x; B80='y; C80='z; D80='Vector; A81(CenterX)==OuterTailHingeXPosition; B81(CenterY)=0; C81(CenterZ)==OuterTailHingeZPosition; D81(Center)==vector(CenterX; CenterY; CenterZ); A82='TailAxisVector; A83='x; B83='y; C83='z; D83='Axis; A84(TailAxisX)==sin(VerticalPlaneAngle); B84(TailAxisY)=0; C84(TailAxisZ)==cos(VerticalPlaneAngle); D84(TailAxisVector)==vector(TailAxisX; TailAxisY; TailAxisZ); A85='Angle; B85='Rotation; C85='RotatedPoint; A86(TailRotationAngle)==180 - HorizontalPlaneAngle - DefaultTailAngle; B86(TailRotationObject)==rotation(TailAxisVector; TailRotationAngle); C86(RotatedPoint)==Center + TailRotationObject * (Point - Center); A87='Tail; A88='x; B88='y; C88='z; A89(TailXPosition)==.RotatedPoint.x; B89(TailYPosition)==.RotatedPoint.y; C89(TailZPosition)==.RotatedPoint.z; A90='TailBoomTriangularBraceZAxisAngle; B90(TailBoomTriangularBraceZAxisAngle)==asin(TailYPosition / TailBoomTriangularBraceWidth); A91='----------; B91='----------; C91='----------; A92='Placement; A93='TailAssembly; A94='x; B94='y; C94='z; A95(TailAssemblyX)==TailHingeJunctionChamfer * cos(180 - HorizontalPlaneAngle); B95(TailAssemblyY)==TailHingeJunctionChamfer * sin(-(180 - HorizontalPlaneAngle)); C95(TailAssemblyZ)=0; A96='Base; B96='Axis; C96='Angle; A97(TailAssemblyBase)==vector(TailAssemblyX; TailAssemblyY; TailAssemblyZ); B97(TailAssemblyAxis)==vector(0; 0; -1); C97(TailAssemblyAngle)==180 - HorizontalPlaneAngle; +44 more cells
FEATURE [Spreadsheet::Sheet] LowEndStop
  cells = A1='Inputs; A2='Spreadsheet; A3='RotorDiskRadius; B3='FlatMetalThickness; C3='YawPipeDiameter; A4(RotorDiskRadius)==Spreadsheet.RotorDiskRadius; B4(FlatMetalThickness)==Spreadsheet.FlatMetalThickness; C4(YawPipeDiameter)==Spreadsheet.YawPipeDiameter; A5='VerticalPlaneAngle; A6(VerticalPlaneAngle)==Spreadsheet.VerticalPlaneAngle; A7='YawBearing; A8='CanSideExtendToMiddleOfYawBearingPipe; A9(CanSideExtendToMiddleOfYawBearingPipe)==YawBearing.CanSideExtendToMiddleOfYawBearingPipe; A10='Tail; A11='TailBoomTriangularBraceWidth; B11='OuterTailHingeParentPlacement; C11='TailAssemblyAngle; A12(TailBoomTriangularBraceWidth)==Tail.TailBoomTriangularBraceWidth; B12(OuterTailHingeParentPlacement)==Tail.OuterTailHingeParentPlacement; C12(TailAssemblyAngle)==Tail.TailAssemblyAngle; A13='HingeOuterPipeRadius; A14(HingeOuterPipeRadius)==Tail.HingeOuterPipeRadius; A15='Calculated; A16='YawPipeRadius; A17(YawPipeRadius)==YawPipeDiameter / 2; A18='Low End Stop; A19='LowEndStopZ; B19(LowEndStopZ)==TailBoomTriangularBraceWidth - FlatMetalThickness; A20='LowEndStopBase; B20(LowEndStopBase)==vector(0; 0; LowEndStopZ); A21='Low End Stop Plane, Yaw Bearing Cylinder, Ellipse of Intersection; A22='OuterLowEndStopWidth; B22='LowEndStopYawBearingOverlap; C22='LowEndStopWidth; A23(OuterLowEndStopWidth)==HingeOuterPipeRadius * 0.5; B23(LowEndStopYawBearingOverlap)==floor(YawPipeDiameter / 6); C23(LowEndStopWidth)==HingeOuterPipeRadius + OuterLowEndStopWidth; A24='LowEndStopTailAssemblyPlacementAxisAligned; B24='LowEndStopTailAssemblyBase; A25(LowEndStopTailAssemblyPlacementAxisAligned)==OuterTailHingeParentPlacement * placement(LowEndStopBase; rotation(vector(0; 0; 0); 0)); B25(LowEndStopTailAssemblyBase)==OuterTailHingeParentPlacement * LowEndStopBase; A26='AlignLowEndStopWithXAxis; B26='LowEndStopTailAssemblyBaseAxisAligned; A27(AlignLowEndStopWithXAxis)==placement(vector(0; 0; 0); vector(0; 0; 1); TailAssemblyAngle); B27(LowEndStopTailAssemblyBaseAxisAligned)==AlignLowEndStopWithXAxis * LowEndStopTailAssemblyBase; A28='Vn; A29(Vn)==.AlignLowEndStopWithXAxis.Rotation * .LowEndStopTailAssemblyPlacementAxisAligned.Rotation * vector(0; 0; 1); A30='LowEndStopPlaneDistance (d); A31(LowEndStopPlaneDistance)==.Vn * LowEndStopTailAssemblyBaseAxisAligned; A32='ZeroAngleZ; B32='PiAngleZ; A33(ZeroAngleZ)==(LowEndStopPlaneDistance - .Vn.x * YawPipeRadius * cos(0)) / .Vn.z; B33(PiAngleZ)==(LowEndStopPlaneDistance - .Vn.x * YawPipeRadius * cos(180)) / .Vn.z; A34='ZeroAnglePoint; B34='PiAnglePoint; A35(ZeroAnglePoint)==vector(YawPipeRadius; 0; ZeroAngleZ); B35(PiAnglePoint)==vector(-YawPipeRadius; 0; PiAngleZ); A36='MajorAxis; B36='SemiMajorAxisLength; C36='XDownScaleFactor; A37(MajorAxis)==ZeroAnglePoint - PiAnglePoint; B37(SemiMajorAxisLength)==.MajorAxis.Length / 2; C37(XDownScaleFactor)==YawPipeRadius / SemiMajorAxisLength; A38='ScaledDownLowEndStopX; A39(ScaledDownLowEndStopX)==.LowEndStopTailAssemblyBaseAxisAligned.x * XDownScaleFactor; A40='SlopeOfTangentLine; A41(SlopeOfTangentLine)==YawPipeRadius / sqrt(-(YawPipeRadius ^ 2) + ScaledDownLowEndStopX ^ 2); A42='TangentPointX2d; B42='TangentPointY2d; A43(TangentPointX2d)==SlopeOfTangentLine * YawPipeRadius / sqrt(1 + SlopeOfTangentLine ^ 2); B43(TangentPointY2d)==SlopeOfTangentLine * TangentPointX2d - YawPipeRadius * sqrt(1 + SlopeOfTangentLine ^ 2); A44='XUpScaleFactor; B44='TangentPointX; C44='TangentPointY; A45(XUpScaleFactor)==1 / XDownScaleFactor; B45(TangentPointX)==XUpScaleFactor * TangentPointX2d; C45(TangentPointZ)==(LowEndStopPlaneDistance - .Vn.x * TangentPointX) / .Vn.z; A46='AxisAlignedTangentPoint; A47(AxisAlignedTangentPoint)==vector(TangentPointX; TangentPointY2d; TangentPointZ); A48='Point on Yaw Bearing cylinder where Low End Stop touches it; A49='TangentPoint; A50(TangentPoint)==minvert(AlignLowEndStopWithXAxis) * AxisAlignedTangentPoint; A51='VectorTowardsLongEnd; B51='TangentPointLowEndStopLocal; C51='LowEndStopAngle; A52(VectorTowardsLongEnd)==vector(0; -1; 0); B52(TangentPointLowEndStopLocal)==minvert(.LowEndStopTailAssemblyPlacementAxisAligned) * TangentPoint; C52(LowEndStopAngle)==acos(.TangentPointLowEndStopLocal * .VectorTowardsLongEnd / (.TangentPointLowEndStopLocal.Length * .VectorTowardsLongEnd.Length)); A53='LowEndStopPlacement; B53='LowEndStopLengthScaleFactor; C53='LowEndStopLength; A54(LowEndStopPlacement)==placement(LowEndStopBase; rotation(vector(0; 0; -1); LowEndStopAngle)); B54(LowEndStopLengthScaleFactor)==RotorDiskRadius < 187.5 ? 1.15 : (CanSideExtendToMiddleOfYawBearingPipe == True ? 1 : 1.1); C54(LowEndStopLength)==.TangentPointLowEndStopLocal.Length * LowEndStopLengthScaleFactor; A55='Extend High End Stop to Low End Stop; A56='VectorTowardsHighEndStop; B56='LowEndStopTailAssemblyPlacement; C56='LowEndStopBottomLeftPoint; A57(VectorTowardsHighEndStop)==vector(-1; 0; 0); B57(LowEndStopTailAssemblyPlacement)==OuterTailHingeParentPlacement * LowEndStopPlacement; C57(LowEndStopBottomLeftPoint)==LowEndStopTailAssemblyPlacement * vector(-LowEndStopYawBearingOverlap; 0; 0); A58='LeftPerpendicularLowEndStopPlane; A59='NormalVector; B59='Distance; A60(LeftPerpendicularLowEndStopPlaneNormalVector)==.LowEndStopTailAssemblyPlacement.Rotation * VectorTowardsHighEndStop; B60(LeftPerpendicularLowEndStopPlaneDistance)==.LeftPerpendicularLowEndStopPlaneNormalVector * .LowEndStopBottomLeftPoint * -1; A61='LowerLowEndStopPlane; A62='NormalVector; B62='Distance; A63(LowerLowEndStopPlaneNormalVector)==.LowEndStopTailAssemblyPlacement.Rotation * vector(0; 0; 1); B63(LowerLowEndStopPlaneDistance)==.LowerLowEndStopPlaneNormalVector * LowEndStopBottomLeftPoint * -1
FEATURE [Spreadsheet::Sheet] HighEndStop
  cells = A1='Inputs; A2='Spreadsheet; A3='FlatMetalThickness; B3='BoomPipeDiameter; C3='YawPipeDiameter; A4(FlatMetalThickness)==Spreadsheet.FlatMetalThickness; B4(BoomPipeDiameter)==Spreadsheet.BoomPipeDiameter; C4(YawPipeDiameter)==Spreadsheet.YawPipeDiameter; A5='VerticalPlaneAngle; B5='HorizontalPlaneAngle; C5='BoomLength; A6(VerticalPlaneAngle)==Spreadsheet.VerticalPlaneAngle; B6(HorizontalPlaneAngle)==Spreadsheet.HorizontalPlaneAngle; C6(BoomLength)==Spreadsheet.BoomLength; A7='YawBearing; A8='YawPipeProjectedLength; A9(YawPipeProjectedLength)==YawBearing.YawPipeProjectedLength; A10='Tail; A11='TailHingeJunctionChamfer; B11='OuterTailHingeParentPlacement; C11='TailPlacement; A12(TailHingeJunctionChamfer)==Tail.TailHingeJunctionChamfer; B12(OuterTailHingeParentPlacement)==Tail.OuterTailHingeParentPlacement; C12(TailPlacement)==Tail.TailPlacement; A13='OuterTailHingeBase; B13='TailAssemblyPlacement; C13='HingeOuterPipeDiameter; A14(OuterTailHingeBase)==Tail.OuterTailHingeBase; B14(TailAssemblyPlacement)==Tail.TailAssemblyPlacement; C14(HingeOuterPipeDiameter)==Tail.HingeOuterPipeDiameter; A15='LowEndStop; A16='LeftPerpendicularLowEndStopPlaneNormalVector; B16='LeftPerpendicularLowEndStopPlaneDistance; A17(LeftPerpendicularLowEndStopPlaneNormalVector)==LowEndStop.LeftPerpendicularLowEndStopPlaneNormalVector; B17(LeftPerpendicularLowEndStopPlaneDistance)==LowEndStop.LeftPerpendicularLowEndStopPlaneDistance; A18='LowerLowEndStopPlaneNormalVector; B18='LowerLowEndStopPlaneDistance; A19(LowerLowEndStopPlaneNormalVector)==LowEndStop.LowerLowEndStopPlaneNormalVector; B19(LowerLowEndStopPlaneDistance)==LowEndStop.LowerLowEndStopPlaneDistance; A20='Static; A21='FurlAxis; A22(FurlAxis)==vector(sin(VerticalPlaneAngle); 0; cos(VerticalPlaneAngle)); A23='Calculated; A24='YawPipeRadius; B24='BoomPipeRadius; A25(YawPipeRadius)==YawPipeDiameter / 2; B25(BoomPipeRadius)==BoomPipeDiameter / 2; A26='Placement; A27='TailBoomVaneAssembly; A28='x; B28='y; C28='z; A29(TailBoomVaneAssemblyX)=0; B29(TailBoomVaneAssemblyY)=0; C29(TailBoomVaneAssemblyZ)=0; A30='Base; B30='Axis; C30='Angle; A31(TailBoomVaneAssemblyBase)==vector(TailBoomVaneAssemblyX; TailBoomVaneAssemblyY; TailBoomVaneAssemblyZ); B31(TailBoomVaneAssemblyAxis)==vector(0; 1; 0); C31(TailBoomVaneAssemblyAngle)=90; A32='Rotation; B32='Placement; A33(TailBoomVaneAssemblyRotation)==rotation(TailBoomVaneAssemblyAxis; TailBoomVaneAssemblyAngle); B33(TailBoomVaneAssemblyPlacement)==placement(TailBoomVaneAssemblyBase; TailBoomVaneAssemblyRotation); A34='HighEndStop; A35='x; B35='y; C35='z; A36(HighEndStopX)==FlatMetalThickness / 2; B36(HighEndStopY)==BoomPipeRadius; C36(HighEndStopZ)=0; A37='Base; B37='Axis; C37='Angle; A38(HighEndStopBase)==vector(HighEndStopX; HighEndStopY; HighEndStopZ); B38(HighEndStopAxis)==vector(0; 1; 0); C38(HighEndStopAngle)=-90; A39='Rotation; B39='Placement; A40(HighEndStopRotation)==rotation(HighEndStopAxis; HighEndStopAngle); B40(HighEndStopPlacement)==placement(HighEndStopBase; HighEndStopRotation); A41='EndOfBoom; A42='x; B42='y; C42='z; A43(EndOfBoomX)=0; B43(EndOfBoomY)=0; C43(EndOfBoomZ)==BoomLength; A44='Base; B44='Axis; C44='Angle; A45(EndOfBoomBase)==vector(EndOfBoomX; EndOfBoomY; EndOfBoomZ); B45(EndOfBoomAxis)==vector(0; 1; 0); C45(EndOfBoomAngle)=-90; A46='Rotation; B46='Placement; A47(EndOfBoomRotation)==rotation(EndOfBoomAxis; EndOfBoomAngle); B47(EndOfBoomPlacement)==placement(EndOfBoomBase; EndOfBoomRotation); A48='----------; B48='----------; C48='----------; A49='Calculated Placement; A50='TailBoomVaneAssemblyParentPlacement; A51(TailBoomVaneAssemblyParentPlacement)==TailPlacement * TailBoomVaneAssemblyPlacement; A52='----------; B52='----------; C52='----------; A53='Maximum Furl Angle; A54='STEP 1:; B54='Find maximum furl plane; A55='AngleBetweenTailAndRotor; A56(AngleBetweenTailAndRotor)==5 deg; A57='Py; B57='Px; A58(Py)==.OuterTailHingeParentPlacement.Base.x * cos(90 deg - AngleBetweenTailAndRotor) + .OuterTailHingeParentPlacement.Base.y; B58(Px)==-1 * .OuterTailHingeParentPlacement.Base.x * sin(90 deg - AngleBetweenTailAndRotor) + .OuterTailHingeParentPlacement.Base.x; A59='slope; B59='xIntercept; C59='NormalVectorOfMaximumFurlPlane; A60(slope)==(Px - .OuterTailHingeParentPlacement.Base.x) / (Py - .OuterTailHingeParentPlacement.Base.y); B60(xIntercept)==Px - slope * Py; C60(NormalVectorOfMaximumFurlPlane)==vector(-1; slope; 0); A61='STEP 2:; B61='Find plane of rotation for boom; A62='EndOfBoom0Rotation; B62='EndOfBoom90Rotation; C62='EndOfBoom180Rotation; D62='EndOfBoom270Rotation; A63(EndOfBoom0Rotation)==rotation(FurlAxis; 0 deg); B63(EndOfBoom90Rotation)==rotation(FurlAxis; 90 deg); C63(EndOfBoom180Rotation)==rotation(FurlAxis; 180 deg); D63(EndOfBoom270Rotation)==rotation(FurlAxis; 270 deg); A64='EndOfBoom0Placement; B64='EndOfBoom90Placement; C64='EndOfBoom180Placement; D64='EndOfBoom270Placement; A65(EndOfBoom0Placement)==placement(.OuterTailHingeBase - EndOfBoom0Rotation * .OuterTailHingeBase; EndOfBoom0Rotation); B65(EndOfBoom90Placement)==placement(.OuterTailHingeBase - EndOfBoom90Rotation * .OuterTailHingeBase; EndOfBoom90Rotation); C65(EndOfBoom180Placement)==placement(.OuterTailHingeBase - EndOfBoom180Rotation * .OuterTailHingeBase; EndOfBoom180Rotation); D65(EndOfBoom270Placement)==placement(.OuterTailHingeBase - EndOfBoom270Rotation * .OuterTailHingeBase; EndOfBoom270Rotation); A66='FurledEndOfBoom0Placement; B66='FurledEndOfBoom90Placement; C66='FurledEndOfBoom180Placement; D66='FurledEndOfBoom270Placement; A67(FurledEndOfBoom0Placement)==TailAssemblyPlacement * EndOfBoom0Placement * TailBoomVaneAssemblyParentPlacement * EndOfBoomPlacement; B67(FurledEndOfBoom90Placement)==TailAssemblyPlacement * EndOfBoom90Placement * TailBoomVaneAssemblyParentPlacement * EndOfBoomPlacement; C67(FurledEndOfBoom180Placement)==TailAssemblyPlacement * EndOfBoom180Placement * TailBoomVaneAssemblyParentPlacement * EndOfBoomPlacement; D67(FurledEndOfBoom270Placement)==TailAssemblyPlacement * EndOfBoom270Placement * TailBoomVaneAssemblyParentPlacement * EndOfBoomPlacement; A68='Axis1; B68='Axis2; A69(Axis1)==.FurledEndOfBoom180Placement.Base - .FurledEndOfBoom0Placement.Base; B69(Axis2)==.FurledEndOfBoom270Placement.Base - .FurledEndOfBoom90Placement.Base; A70='Vg; B70='Axis1 × Axis2; A71(Vg)==vector(.Axis1.y * .Axis2.z - .Axis1.z * .Axis2.y; .Axis1.z * .Axis2.x - .Axis1.x * .Axis2.z; .Axis1.x * .Axis2.y - .Axis1.y * .Axis2.x); B71='Cross Product; A72='Vh; B72='Normalize Vg; A73(Vh)==Vg / .Vg.Length; A74='BoomRotationPlaneDistance (d); A75(BoomRotationPlaneDistance)==-Vh * .FurledEndOfBoom0Placement.Base; A76='STEP 3:; B76='Find sphere containing the plane of rotation for the boom; A77='CenterOfSphere; B77='Radius; A78(CenterOfSphere)==.FurledEndOfBoom0Placement.Base + Axis1 / 2; B78(Radius)==.Axis1.Length / 2; A79='STEP 4:; B79='Find line formed by the intersection of maximum furl plane and plane of rotation for boom; A80='xLineOrigin; B80='yLineOrigin; C80='zLineOrigin; A81(xLineOrigin)==.CenterOfSphere.x - Radius * 1.1; B81(yLineOrigin)==(xLineOrigin - xIntercept) / slope; C81(zLineOrigin)==-(BoomRotationPlaneDistance + .Vh.x * xLineOrigin + .Vh.y * yLineOrigin) / .Vh.z; A82='LineOrigin; A83(LineOrigin)==vector(xLineOrigin; yLineOrigin; zLineOrigin); A84='DirectionVector; B84='Vh × NormalVectorOfMaximumFurlPlane; A85(DirectionVector)==vector(.Vh.y * .NormalVectorOfMaximumFurlPlane.z - .Vh.z * .NormalVectorOfMaximumFurlPlane.y; .Vh.z * .NormalVectorOfMaximumFurlPlane.x - .Vh.x * .NormalVectorOfMaximumFurlPlane.z; .Vh.x * .NormalVectorOfMaximumFurlPlane.y - .Vh.y * .NormalVectorOfMaximumFurlPlane.x); B85='Cross Product; A86='NormalizedDirectionVector; A87(NormalizedDirectionVector)==.DirectionVector / .DirectionVector.Length; A88='STEP 5:; B88='Find intersection point on the line and sphere closest to boom starting point; A89='ValueOfTForPointOnLineClosestToCenterOfSphere; B89='PointOnLineClosestToCenterOfSphere; A90(ValueOfTForPointOnLineClosestToCenterOfSphere)==(CenterOfSphere - LineOrigin) * NormalizedDirectionVector; B90(PointOnLineClosestToCenterOfSphere)==LineOrigin + ValueOfTForPointOnLineClosestToCenterOfSphere * NormalizedDirectionVector; A91='yVector; B91='yDistance; C91='xDistance; A92(yVector)==CenterOfSphere - PointOnLineClosestToCenterOfSphere; B92(yDistance)==.yVector.Length; C92(xDistance)==sqrt(Radius ^ 2 - yDistance ^ 2); A93='ValueOfTForFarthestIntersectionPoint; B93='FarthestIntersectionPoint; A94(ValueOfTForFarthestIntersectionPoint)==ValueOfTForPointOnLineClosestToCenterOfSphere + xDistance; B94(FarthestIntersectionPoint)==LineOrigin + ValueOfTForFarthestIntersectionPoint * NormalizedDirectionVector; +119 more cells
FEATURE [Spreadsheet::Sheet] WindTurbine
  cells = A1='Inputs; A2='Spreadsheet; A3='RotorDiskRadius; B3='FlatMetalThickness; A4(RotorDiskRadius)==Spreadsheet.RotorDiskRadius; B4(FlatMetalThickness)==Spreadsheet.FlatMetalThickness; A5='VerticalPlaneAngle; B5='HorizontalPlaneAngle; C5='Offset; A6(VerticalPlaneAngle)==Spreadsheet.VerticalPlaneAngle; B6(HorizontalPlaneAngle)==Spreadsheet.HorizontalPlaneAngle; C6(Offset)==Spreadsheet.Offset; A7='YawPipeDiameter; B7='MetalLengthL; C7='MetalThicknessL; A8(YawPipeDiameter)==Spreadsheet.YawPipeDiameter; B8(MetalLengthL)==Spreadsheet.MetalLengthL; C8(MetalThicknessL)==Spreadsheet.MetalThicknessL; A9='Alternator; A10='FrameZ; B10='HShapeChannelSectionHeight; C10='StarShapeChannelSectionHeight; A11(FrameZ)==Alternator.FrameZ; B11(HShapeChannelSectionHeight)==Alternator.HH; C11(StarShapeChannelSectionHeight)==Alternator.B; A12='AlternatorTiltAngle; A13(AlternatorTiltAngle)==Alternator.AlternatorTiltAngle; A14='T Shape; A15='k; A16(k)==Alternator.k; A17='YawBearing; A18='TopAngle; B18='SideWidth; C18='LargeYawBearingXOffset; A19(TopAngle)==YawBearing.TopAngle; B19(SideWidth)==YawBearing.SideWidth; C19(LargeYawBearingXOffset)==YawBearing.LargeYawBearingXOffset; A20='HighEndStop; A21='YawPipeLength; A22(YawPipeLength)==HighEndStop.YawPipeLength; A23='Calculated; A24='YawPipeRadius; B24='YawBearingZPosition; A25(YawPipeRadius)==YawPipeDiameter / 2; B25(YawBearingZPosition)==-Offset; A26='SmallYawBearing; A27='Angle; A28(SmallYawBearingAngle)==90 deg; A29='x; B29='y; C29='z; A30(SmallYawBearingX)==-FrameZ - YawPipeRadius - k + MetalLengthL - MetalThicknessL; B30(SmallYawBearingY)==(YawPipeLength - FlatMetalThickness) / 2; C30(SmallYawBearingZ)==YawBearingZPosition; A31='LargeYawBearing; A32='SpaceBetweenMiddleBracketAndTopEndBracket; B32='LargeYawBearingYAdjustment; C32='LargeYawBearingYPreAlternatorTilt; A33(SpaceBetweenMiddleBracketAndTopEndBracket)==StarShapeChannelSectionHeight / 2 - MetalLengthL / 2; B33(LargeYawBearingYAdjustment)==(SpaceBetweenMiddleBracketAndTopEndBracket - (SideWidth + FlatMetalThickness)) / 2; C33(LargeYawBearingYPreAlternatorTilt)==MetalLengthL / 2 + SideWidth + LargeYawBearingYAdjustment; A34='LargeYawBearingZPosition; B34='LargeYawBearingXPosition; C34='YawBearingXOffset; D34='AlternatorLinkYOffset; A35(LargeYawBearingZPosition)==YawBearingZPosition; B35(LargeYawBearingXPosition)==LargeYawBearingZPosition - FrameZ + LargeYawBearingXOffset; C35(YawBearingXOffset)==RotorDiskRadius < 187.5 ? SmallYawBearingX : LargeYawBearingX; D35(AlternatorLinkYOffset)==-sin(AlternatorTiltAngle) * YawBearingXOffset; A36='ChannelSectionHeight; B36='HShapeYawBearingY; C36='StarShapeYawBearingY; A37(ChannelSectionHeight)==RotorDiskRadius < 275 ? HShapeChannelSectionHeight : StarShapeChannelSectionHeight; B37(HShapeYawBearingY)==ChannelSectionHeight * 0.25; C37(StarShapeYawBearingY)==LargeYawBearingYPreAlternatorTilt; A38='Angle; A39(LargeYawBearingAngle)==-TopAngle; A40='x; B40='y; C40='z; A41(LargeYawBearingX)==LargeYawBearingXPosition; B41(LargeYawBearingY)==RotorDiskRadius < 275 ? HShapeYawBearingY : StarShapeYawBearingY; C41(LargeYawBearingZ)==LargeYawBearingZPosition; A42='SmallTailHinge; A43='x; B43='y; C43='z; A44(SmallTailHingeX)==SmallYawBearingX; B44(SmallTailHingeY)==-SmallYawBearingY - FlatMetalThickness; C44(SmallTailHingeZ)==SmallYawBearingZ; A45='LargeTailHinge; A46='x; B46='y; C46='z; A47(LargeTailHingeX)==LargeYawBearingX; B47(LargeTailHingeY)==-(YawPipeLength - LargeYawBearingY); C47(LargeTailHingeZ)==LargeYawBearingZ; A48='VerticalDistanceFromCenter; B48='Vertical distance of Yaw Bearing from Center of Hub; A49='SmallVerticalDistanceFromCenter; B49(SmallVerticalDistanceFromCenter)==(YawPipeLength + FlatMetalThickness) / 2; A50='LargeVerticalDistanceFromCenter; B50(LargeVerticalDistanceFromCenter)==LargeYawBearingY; A51='VerticalDistanceFromCenter; B51(VerticalDistanceFromCenter)==RotorDiskRadius < 187.5 ? SmallVerticalDistanceFromCenter : LargeVerticalDistanceFromCenter; A52='AlternatorXoffset; B52(AlternatorXoffset)==cos(90 deg - AlternatorTiltAngle) * VerticalDistanceFromCenter; A53='Placement; A54='YawBearing; A55='x; B55='y; C55='z; A56(YawBearingX)==YawBearingXOffset; B56(YawBearingY)==RotorDiskRadius < 187.5 ? SmallYawBearingY : LargeYawBearingY; C56(YawBearingZ)==RotorDiskRadius < 187.5 ? SmallYawBearingZ : LargeYawBearingZ; A57='Base; B57='Axis; C57='Angle; A58(YawBearingBase)==vector(YawBearingX; YawBearingY; YawBearingZ); B58(YawBearingAxis)==vector(0; 1; 0); C58(YawBearingAngle)==RotorDiskRadius < 187.5 ? SmallYawBearingAngle : LargeYawBearingAngle; A59='Rotation; B59='Placement; A60(YawBearingRotation)==rotation(YawBearingAxis; YawBearingAngle); B60(YawBearingPlacement)==placement(YawBearingBase; YawBearingRotation); A61='AlternatorLink; A62='x; B62='y; C62='z; A63(AlternatorLinkX)==YawBearingX - YawBearingX * cos(AlternatorTiltAngle) + AlternatorXoffset; B63(AlternatorLinkY)==AlternatorLinkYOffset; C63(AlternatorLinkZ)=0; A64='Base; B64='Axis; C64='Angle; A65(AlternatorLinkBase)==vector(AlternatorLinkX; AlternatorLinkY; AlternatorLinkZ); B65(AlternatorLinkAxis)==vector(0; 0; 1); C65(AlternatorLinkAngle)==AlternatorTiltAngle; A66='Rotation; B66='Placement; A67(AlternatorLinkRotation)==rotation(AlternatorLinkAxis; AlternatorLinkAngle); B67(AlternatorLinkPlacement)==placement(AlternatorLinkBase; AlternatorLinkRotation); A68='TailAssemblyLink; A69='x; B69='y; C69='z; A70(TailAssemblyLinkX)==RotorDiskRadius < 187.5 ? SmallTailHingeX : LargeTailHingeX; B70(TailAssemblyLinkY)==RotorDiskRadius < 187.5 ? SmallTailHingeY : LargeTailHingeY; C70(TailAssemblyLinkZ)==RotorDiskRadius < 187.5 ? SmallTailHingeZ : LargeTailHingeZ; A71='Base; B71='Axis; C71='Angle; A72(TailAssemblyLinkBase)==vector(TailAssemblyLinkX; TailAssemblyLinkY; TailAssemblyLinkZ); B72(TailAssemblyLinkAxis)==vector(0.58; 0.58; 0.58); C72(TailAssemblyLinkAngle)==240 deg; A73='Rotation; B73='Placement; A74(TailAssemblyLinkRotation)==rotation(TailAssemblyLinkAxis; TailAssemblyLinkAngle); B74(TailAssemblyLinkPlacement)==placement(TailAssemblyLinkBase; TailAssemblyLinkRotation)
